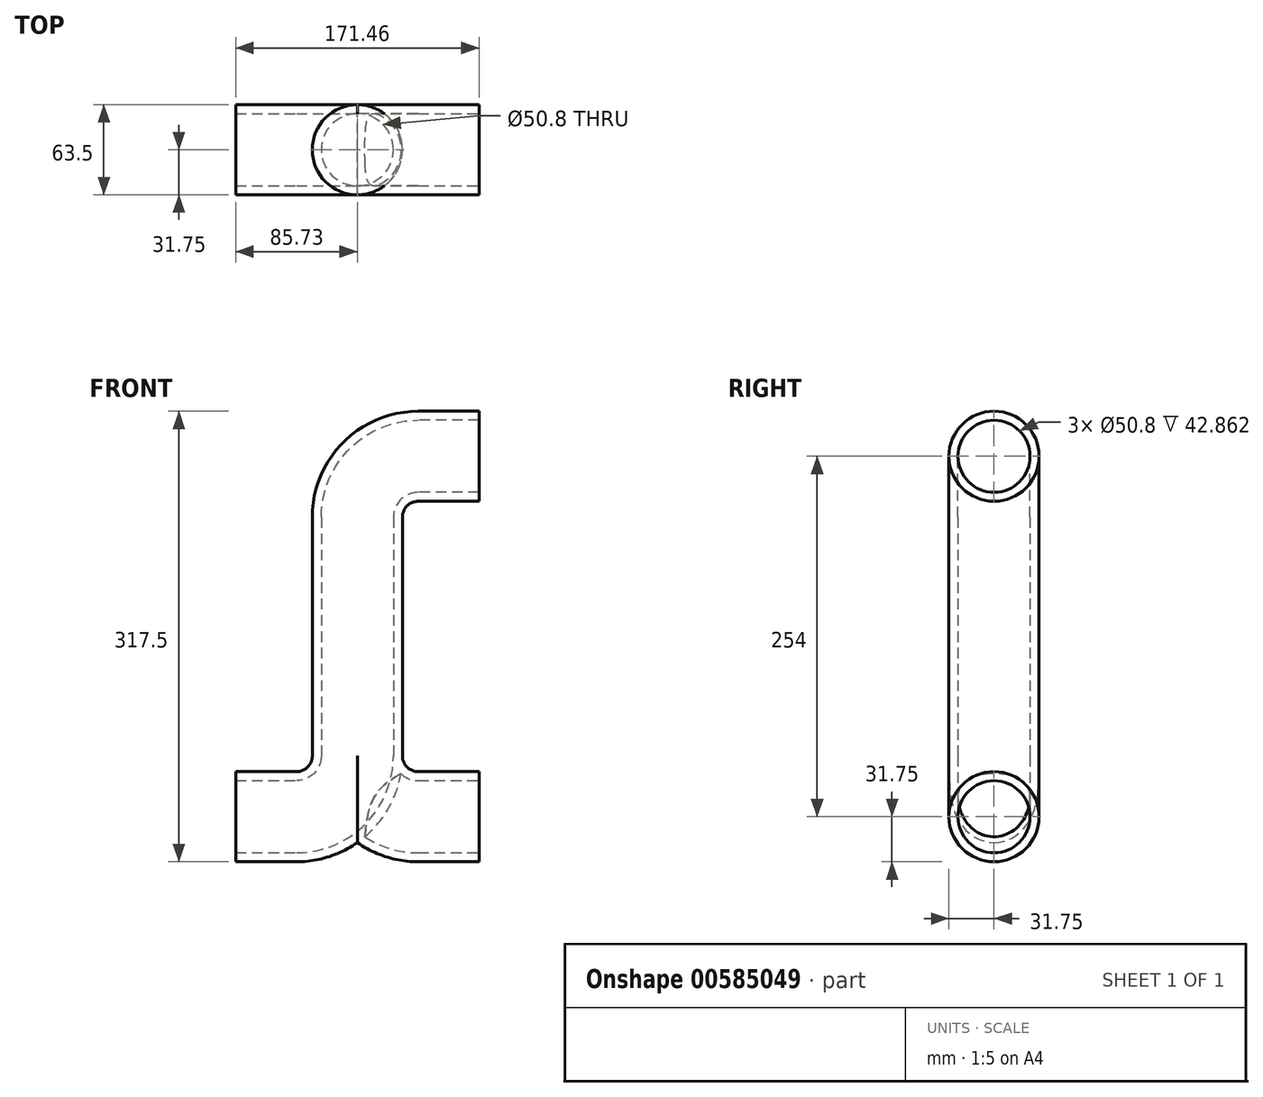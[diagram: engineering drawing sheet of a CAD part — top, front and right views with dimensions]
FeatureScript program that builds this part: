
annotation { "Feature Type Name" : "Feature", "Feature Type Description" : "" }
export const myFeature = defineFeature(function(context is Context, id is Id, definition is map)
    precondition{}
    {
        {
            var Q0;
            Q0=qCreatedBy(makeId("Right.planeOp"),FACE);
            cPlane(context, id + "F0", {"entities" : qUnion([Q0]), "cplaneType" : CPlaneType.OFFSET, "offset" : 85.72 * mm, "width" : 152.4 * mm, "height" : 152.4 * mm});
        }
        {
            var Q0;
            Q0=qCreatedBy(makeId("Front.planeOp"),FACE);
            var sketch = newSketch(context, id + "F1", { "sketchPlane" : qUnion([Q0])});
            skLineSegment(sketch, "E0", {"start": v(0, 42.86) * mm, "end": v(0, 211.14) * mm});
            skLineSegment(sketch, "E1", {"start": v(-85.73, 0) * mm, "end": v(-42.86, 0) * mm, "construction": true});
            skLineSegment(sketch, "E2", {"start": v(42.86, 254) * mm, "end": v(85.72, 254) * mm});
            skLineSegment(sketch, "E3.bottom", {"start": v(-42.86, 42.86) * mm, "end": v(42.86, 42.86) * mm, "construction": true});
            skLineSegment(sketch, "E3.top", {"start": v(-42.86, -42.86) * mm, "end": v(42.86, -42.86) * mm, "construction": true});
            skLineSegment(sketch, "E3.left", {"start": v(-42.86, 42.86) * mm, "end": v(-42.86, -42.86) * mm, "construction": true});
            skLineSegment(sketch, "E3.right", {"start": v(42.86, 42.86) * mm, "end": v(42.86, -42.86) * mm, "construction": true});
            skPoint(sketch, "E3.middle", {"position": v(0, 0) * mm});
            skArc(sketch, "E4", {"start": v(-42.86, 0) * mm, "mid": v(-12.55, 12.55) * mm, "end": v(0, 42.86) * mm, "construction": true});
            skArc(sketch, "E5", {"start": v(0, 42.86) * mm, "mid": v(12.55, 12.55) * mm, "end": v(42.86, 0) * mm});
            skLineSegment(sketch, "E6.bottom", {"start": v(42.86, 211.14) * mm, "end": v(-42.86, 211.14) * mm, "construction": true});
            skLineSegment(sketch, "E6.top", {"start": v(42.86, 296.86) * mm, "end": v(-42.86, 296.86) * mm, "construction": true});
            skLineSegment(sketch, "E6.left", {"start": v(42.86, 211.14) * mm, "end": v(42.86, 296.86) * mm, "construction": true});
            skLineSegment(sketch, "E6.right", {"start": v(-42.86, 211.14) * mm, "end": v(-42.86, 296.86) * mm, "construction": true});
            skPoint(sketch, "E6.middle", {"position": v(0, 254) * mm});
            skPoint(sketch, "E6.cornerSnap0", {"position": v(42.86, 254) * mm});
            skArc(sketch, "E7", {"start": v(42.86, 254) * mm, "mid": v(12.55, 241.45) * mm, "end": v(0, 211.14) * mm});
            skLineSegment(sketch, "E8.trimOffspring", {"start": v(42.86, 0) * mm, "end": v(85.73, 0) * mm});
            skSolve(sketch);
        }
        {
            var Q0;
            Q0=qCreatedBy(id+"F0.planeOp",FACE);
            var sketch = newSketch(context, id + "F2", { "sketchPlane" : qUnion([Q0])});
            skCircle(sketch, "E9", {"center": v(0, 254) * mm, "radius": 25.4 * mm});
            skCircle(sketch, "E10.0", {"center": v(0, 254) * mm, "radius": 31.75 * mm});
            skSolve(sketch);
        }
        {
            var Q0;
            Q0=makeQuery(id+"F2.imprint","IMPRINT",FACE,{"disambiguationData":[TD([[makeQuery(id+"F2.imprint","IMPRINT",EDGE,{"derivedFrom":sQuery(id+"F2.wireOp",EDGE,"E9")}),-1.0]])]});
            var Q1;
            Q1 = qConstructionFilter(qBodyType(qCreatedBy(id + "F1" ,EDGE), BodyType.WIRE), ConstructionObject.NO);
            sweep(context, id + "F3", {"profiles" : qUnion([Q0]), "path" : qUnion([Q1])});
        }
        {
            var Q0;
            Q0=qCreatedBy(makeId("Front.planeOp"),FACE);
            var sketch = newSketch(context, id + "F4", { "sketchPlane" : qUnion([Q0])});
            skLineSegment(sketch, "E11", {"start": v(-85.73, 0) * mm, "end": v(-42.86, 0) * mm});
            skArc(sketch, "E12", {"start": v(-42.86, 0) * mm, "mid": v(-12.55, 12.55) * mm, "end": v(0, 42.86) * mm});
            skLineSegment(sketch, "E13", {"start": v(-42.86, 0) * mm, "end": v(0, 0) * mm, "construction": true});
            skLineSegment(sketch, "E14", {"start": v(0, 0) * mm, "end": v(0, 42.86) * mm, "construction": true});
            skSolve(sketch);
        }
        {
            var Q0;
            Q0=qCreatedBy(makeId("Right.planeOp"),FACE);
            cPlane(context, id + "F5", {"entities" : qUnion([Q0]), "cplaneType" : CPlaneType.OFFSET, "offset" : 85.72 * mm, "oppositeDirection" : true, "width" : 152.4 * mm, "height" : 152.4 * mm});
        }
        {
            var Q0;
            Q0=qCreatedBy(id+"F5.planeOp",FACE);
            var sketch = newSketch(context, id + "F6", { "sketchPlane" : qUnion([Q0])});
            skCircle(sketch, "E15", {"center": v(0, 0) * mm, "radius": 25.4 * mm});
            skCircle(sketch, "E16.0", {"center": v(0, 0) * mm, "radius": 31.75 * mm});
            skSolve(sketch);
        }
        {
            var Q0;
            Q0=makeQuery(id+"F6.imprint","IMPRINT",FACE,{"disambiguationData":[TD([[makeQuery(id+"F6.imprint","IMPRINT",EDGE,{"derivedFrom":sQuery(id+"F6.wireOp",EDGE,"E15")}),-1.0]])]});
            var Q1;
            Q1 = qConstructionFilter(qBodyType(qCreatedBy(id + "F4" ,EDGE), BodyType.WIRE), ConstructionObject.NO);
            sweep(context, id + "F7", {"operationType" : NewBodyOperationType.ADD, "profiles" : qUnion([Q0]), "path" : qUnion([Q1])});
        }
        {
            var Q0;
            Q0=makeQuery(id+"F6.imprint","IMPRINT",FACE,{"disambiguationData":[TD([[makeQuery(id+"F6.imprint","IMPRINT",EDGE,{"derivedFrom":sQuery(id+"F6.wireOp",EDGE,"E15")}),1.0]])]});
            var Q1;
            Q1 = qConstructionFilter(qBodyType(qCreatedBy(id + "F4" ,EDGE), BodyType.WIRE), ConstructionObject.NO);
            sweep(context, id + "F8", {"operationType" : NewBodyOperationType.REMOVE, "profiles" : qUnion([Q0]), "path" : qUnion([Q1])});
        }
    });
